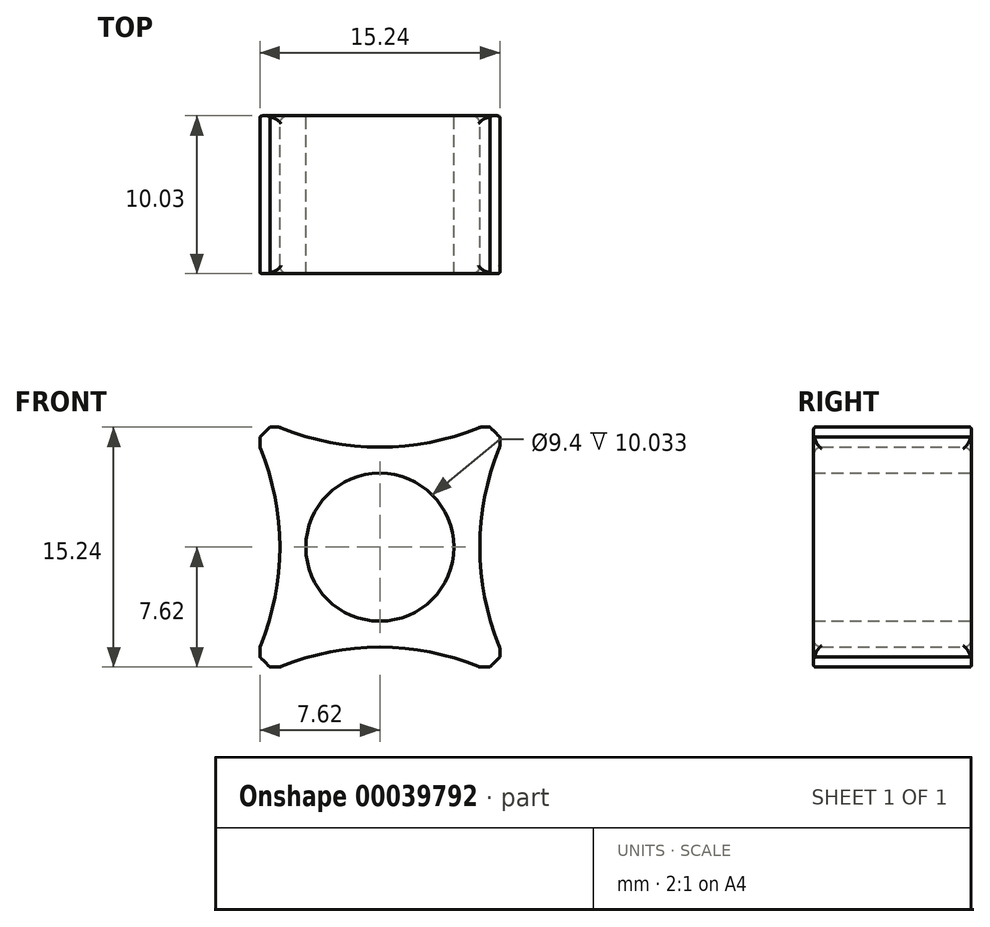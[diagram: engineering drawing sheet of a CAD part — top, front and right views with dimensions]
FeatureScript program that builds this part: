
annotation { "Feature Type Name" : "Feature", "Feature Type Description" : "" }
export const myFeature = defineFeature(function(context is Context, id is Id, definition is map)
    precondition{}
    {
        {
            var Q0;
            Q0=qCreatedBy(makeId("Front.planeOp"),FACE);
            var sketch = newSketch(context, id + "F0", { "sketchPlane" : qUnion([Q0])});
            skLineSegment(sketch, "E0", {"start": v(0, 0) * mm, "end": v(4.06, 0) * mm});
            skPoint(sketch, "E1.0.midPoint", {"position": v(4.06, 0) * mm});
            skLineSegment(sketch, "E2", {"start": v(0, 0) * mm, "end": v(-12.7, 0) * mm});
            skLineSegment(sketch, "E3", {"start": v(12.7, 0) * mm, "end": v(11.43, 0) * mm});
            skLineSegment(sketch, "E4", {"start": v(-12.7, 0) * mm, "end": v(-10.16, 0) * mm});
            skLineSegment(sketch, "E5", {"start": v(-12.7, 0) * mm, "end": v(-11.43, 0) * mm});
            skPoint(sketch, "E6.endSnap0", {"position": v(0, -12.7) * mm});
            skLineSegment(sketch, "E7", {"start": v(0, 0) * mm, "end": v(7.62, 0) * mm});
            skLineSegment(sketch, "E8", {"start": v(0, 0) * mm, "end": v(-7.62, 0) * mm});
            skLineSegment(sketch, "E9", {"start": v(-7.62, 7.62) * mm, "end": v(-7.62, 6.35) * mm, "construction": true});
            skLineSegment(sketch, "E10", {"start": v(-7.62, -6.35) * mm, "end": v(-7.62, -6.99) * mm});
            skLineSegment(sketch, "E11", {"start": v(-7.62, -6.35) * mm, "end": v(-7.62, -7.62) * mm, "construction": true});
            skLineSegment(sketch, "E12", {"start": v(-7.62, -6.99) * mm, "end": v(-7.62, -7.62) * mm, "construction": true});
            skLineSegment(sketch, "E13", {"start": v(-7.62, 7.62) * mm, "end": v(-6.35, 7.62) * mm, "construction": true});
            skLineSegment(sketch, "E14", {"start": v(-6.35, 7.62) * mm, "end": v(-6.99, 7.62) * mm});
            skLineSegment(sketch, "E15", {"start": v(7.62, 7.62) * mm, "end": v(6.35, 7.62) * mm, "construction": true});
            skLineSegment(sketch, "E16", {"start": v(6.35, 7.62) * mm, "end": v(6.98, 7.62) * mm});
            skLineSegment(sketch, "E17", {"start": v(7.62, 7.62) * mm, "end": v(6.98, 7.62) * mm, "construction": true});
            skLineSegment(sketch, "E18", {"start": v(6.35, 7.62) * mm, "end": v(7.62, 7.62) * mm, "construction": true});
            skLineSegment(sketch, "E19", {"start": v(7.62, 6.35) * mm, "end": v(7.62, 7.62) * mm, "construction": true});
            skLineSegment(sketch, "E20", {"start": v(7.62, -7.62) * mm, "end": v(7.62, -6.35) * mm, "construction": true});
            skLineSegment(sketch, "E21", {"start": v(-7.62, -7.62) * mm, "end": v(-6.35, -7.62) * mm, "construction": true});
            skLineSegment(sketch, "E22", {"start": v(-6.35, -7.62) * mm, "end": v(-6.99, -7.62) * mm});
            skLineSegment(sketch, "E23", {"start": v(7.62, -7.62) * mm, "end": v(6.35, -7.62) * mm, "construction": true});
            skLineSegment(sketch, "E24", {"start": v(6.35, -7.62) * mm, "end": v(6.99, -7.62) * mm});
            skLineSegment(sketch, "E25", {"start": v(0, -7.62) * mm, "end": v(0, -6.35) * mm});
            skLineSegment(sketch, "E26", {"start": v(-7.62, 0) * mm, "end": v(-6.35, 0) * mm});
            skLineSegment(sketch, "E27", {"start": v(0, 7.62) * mm, "end": v(0, 6.35) * mm});
            skPoint(sketch, "E27.endSnap0", {"position": v(0, 7.62) * mm});
            skLineSegment(sketch, "E28", {"start": v(7.62, 0) * mm, "end": v(6.35, 0) * mm});
            skArc(sketch, "E29", {"start": v(-7.62, -6.35) * mm, "mid": v(-6.35, 0) * mm, "end": v(-7.62, 6.35) * mm});
            skArc(sketch, "E30", {"start": v(-6.35, 7.62) * mm, "mid": v(0, 6.35) * mm, "end": v(6.35, 7.62) * mm});
            skArc(sketch, "E31", {"start": v(6.35, -7.62) * mm, "mid": v(0, -6.35) * mm, "end": v(-6.35, -7.62) * mm});
            skArc(sketch, "E32", {"start": v(7.62, 6.35) * mm, "mid": v(6.35, 0) * mm, "end": v(7.62, -6.35) * mm});
            skLineSegment(sketch, "E33", {"start": v(-4.06, 0) * mm, "end": v(4.06, 0) * mm});
            skLineSegment(sketch, "E34", {"start": v(-7.62, 6.35) * mm, "end": v(-7.62, -6.35) * mm, "construction": true});
            skLineSegment(sketch, "E35", {"start": v(7.62, 0) * mm, "end": v(10.77, 0) * mm});
            skLineSegment(sketch, "E36", {"start": v(0, 0) * mm, "end": v(10.77, 0) * mm, "construction": true});
            skLineSegment(sketch, "E37", {"start": v(-6.99, 7.62) * mm, "end": v(-7.62, 6.99) * mm});
            skLineSegment(sketch, "E38", {"start": v(-6.99, 7.62) * mm, "end": v(-6.35, 7.62) * mm});
            skLineSegment(sketch, "E39", {"start": v(-7.62, 6.99) * mm, "end": v(-7.62, 6.35) * mm});
            skLineSegment(sketch, "E40", {"start": v(-7.62, -6.99) * mm, "end": v(-6.99, -7.62) * mm});
            skLineSegment(sketch, "E41", {"start": v(-6.99, -7.62) * mm, "end": v(-6.35, -7.62) * mm});
            skLineSegment(sketch, "E42", {"start": v(6.99, -7.62) * mm, "end": v(7.62, -6.99) * mm});
            skLineSegment(sketch, "E43", {"start": v(7.62, -6.99) * mm, "end": v(7.62, -6.35) * mm});
            skLineSegment(sketch, "E44", {"start": v(6.99, -7.62) * mm, "end": v(6.35, -7.62) * mm});
            skLineSegment(sketch, "E45", {"start": v(6.98, 7.62) * mm, "end": v(7.62, 6.99) * mm});
            skLineSegment(sketch, "E46", {"start": v(7.62, 6.99) * mm, "end": v(7.62, 6.35) * mm});
            skLineSegment(sketch, "E47", {"start": v(-7.62, 7.62) * mm, "end": v(7.62, 7.62) * mm, "construction": true});
            skLineSegment(sketch, "E48", {"start": v(0, 0) * mm, "end": v(4.7, 0) * mm});
            skLineSegment(sketch, "E49", {"start": v(0, 0) * mm, "end": v(-4.7, 0) * mm});
            skCircle(sketch, "E50", {"center": v(0, 0) * mm, "radius": 4.7 * mm});
            skLineSegment(sketch, "E51", {"start": v(-6.35, 0) * mm, "end": v(6.35, 0) * mm});
            skLineSegment(sketch, "E52", {"start": v(-6.35, 0) * mm, "end": v(-6.35, -11.23) * mm, "construction": true});
            skLineSegment(sketch, "E53", {"start": v(6.35, 0) * mm, "end": v(6.35, -11.23) * mm, "construction": true});
            skLineSegment(sketch, "E54", {"start": v(-6.35, -11.23) * mm, "end": v(6.35, -11.23) * mm, "construction": true});
            skSolve(sketch);
        }
        {
            var Q0;
            Q0 = qSketchRegion(id + "F0", true);
            extrude(context, id + "F1", {"entities" : qUnion([Q0]), "depth" : 10.03 * mm});
        }
        {
            var Q0;
            Q0=makeQuery(id+"F1.opExtrude","SWEPT_FACE",FACE,{"disambiguationData":[OSD([sQuery(id+"F0.wireOp",EDGE,"E29")])]});
            var Q1;
            Q1=makeQuery(id+"F1.opExtrude","SWEPT_FACE",FACE,{"disambiguationData":[OSD([sQuery(id+"F0.wireOp",EDGE,"E30")])]});
            var Q2;
            Q2=makeQuery(id+"F1.opExtrude","SWEPT_FACE",FACE,{"disambiguationData":[OSD([sQuery(id+"F0.wireOp",EDGE,"E32")])]});
            var Q3;
            Q3=makeQuery(id+"F1.opExtrude","SWEPT_FACE",FACE,{"disambiguationData":[OSD([sQuery(id+"F0.wireOp",EDGE,"E31")])]});
            fillet(context, id + "F2", {"entities" : qUnion([Q0, Q1, Q2, Q3]), "radius" : 0.5 * mm, "tangentPropagation" : true, "allowEdgeOverflow" : false});
        }
    });
